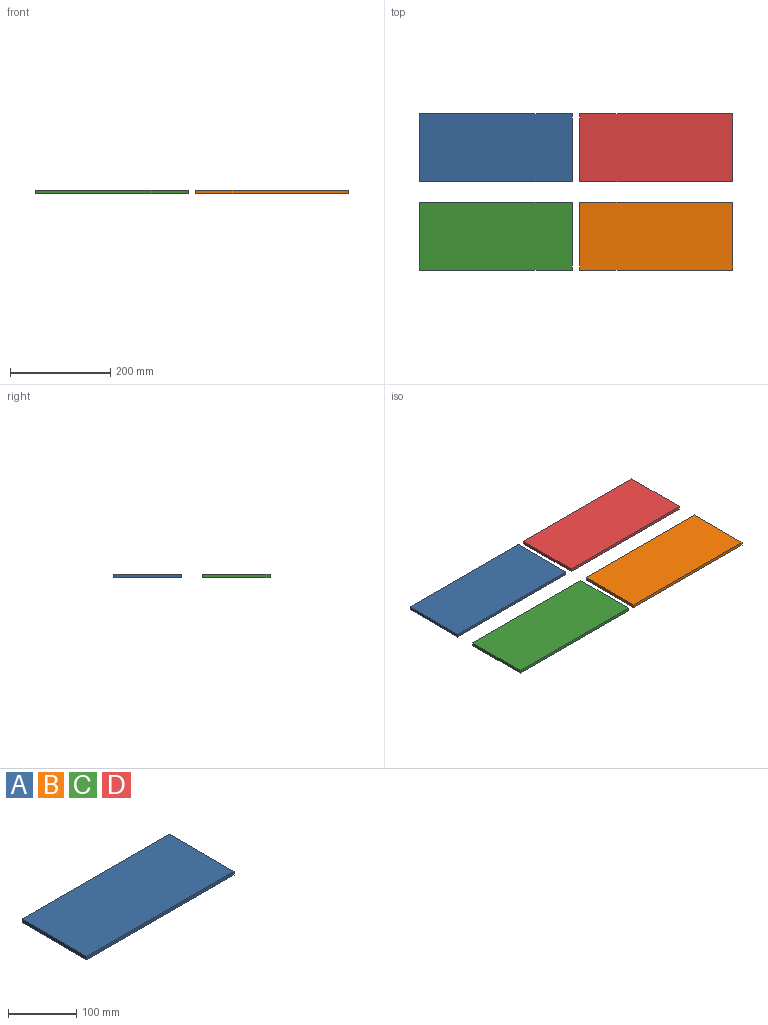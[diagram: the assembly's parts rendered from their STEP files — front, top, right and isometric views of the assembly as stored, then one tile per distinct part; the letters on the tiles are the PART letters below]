
ASSEMBLY  parts=4 mates=7
PART A: 6 faces, bbox 304.8x134.6x6.4 mm
  f0: plane 304.8x6.35mm, normal (0,1,0), area 1935.5mm2, adj f1,f3,f4,f5
  f1: plane 134.62x6.35mm, normal (-1,0,0), area 854.8mm2, adj f0,f2,f4,f5
  f2: plane 304.8x6.35mm, normal (0,-1,0), area 1935.5mm2, adj f1,f3,f4,f5
  f3: plane 134.62x6.35mm, normal (1,0,0), area 854.8mm2, adj f0,f2,f4,f5
  f4: plane 304.8x134.62mm, normal (0,0,1), area 41032.2mm2, adj f0,f1,f2,f3
  f5: plane 304.8x134.62mm, normal (0,0,-1), area 41032.2mm2, adj f0,f1,f2,f3
PART B: same geometry as A
PART C: same geometry as A
PART D: same geometry as A
PLACE A t=(-225.26,81.06,-63.91)mm
PLACE B t=(94.55,-95.28,-63.91)mm
PLACE C t=(-225.26,-95.28,-63.91)mm
PLACE D t=(94.55,81.06,-63.91)mm
MATE planar A.f4 <-> D.f4  axis (0,0,1) through (-225.26,81.06,-57.56)mm
MATE planar B.f1 <-> D.f1  axis (-1,0,0) through (-57.85,-95.28,-60.73)mm
MATE planar C.f4 <-> B.f4  axis (0,0,1) through (-225.26,-95.28,-57.56)mm
MATE planar C.f3 <-> A.f3  axis (1,0,0) through (-72.86,-95.28,-60.73)mm
MATE planar C.f2 <-> B.f2  axis (0,-1,0) through (-225.26,-162.59,-60.73)mm
MATE planar D.f4 <-> C.f4  axis (0,0,1) through (94.55,81.06,-57.56)mm
MATE planar A.f2 <-> D.f2  axis (0,-1,0) through (-72.86,13.75,-60.73)mm
